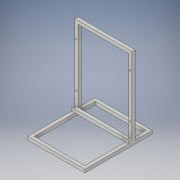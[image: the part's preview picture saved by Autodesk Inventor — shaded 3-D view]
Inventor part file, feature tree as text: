
AUTODESK INVENTOR PART (.ipt)
format: ipt  version: 2019 (Build 230136000, 136)  size: 188,416 bytes
history: native  units: mm
features: extrude x6, sketch x6
ambient origin geometry x8: Origin, YZ Plane, XZ Plane, XY Plane, X Axis, Y Axis, Z Axis, Center Point
bodies: Solid1 (feature_tree)
feature tree (12):
  extrude  "Extrusion1"  Depth=19.0mm
  extrude  "Extrusion2"  Depth=19.0mm
  extrude  "Extrusion3"  Depth=335.0mm
  extrude  "Extrusion4"  Depth=19.0mm
  extrude  "Extrusion5"  Depth=100.0mm
  extrude  "Extrusion6"  Depth=19.0mm
  sketch  "Sketch1"  dims[d2=19.0mm d3=19.0mm]
  sketch  "Sketch3"  dims[d4=19.0mm d5=19.0mm]
  sketch  "Sketch4"  dims[d6=395.0mm d7=335.0mm]
  sketch  "Sketch5"  dims[d8=19.0mm d9=0.0mm d26=19.0mm]
  sketch  "Sketch6"  dims[d27=19.0mm d28=100.0mm]
  sketch  "Sketch7"  dims[d29=460.0mm d30=0.0mm d31=19.0mm d32=316.0mm d33=0.0mm d34=8.0mm d35=8.0mm d36=8.0mm d37=8.0mm d38=9.5mm d39=100.0mm d40=100.0mm d41=9.5mm d42=9.5mm d43=100.0mm d44=100.0mm d45=9.5mm d46=19.0mm d47=0.0mm d48=19.0mm d49=335.0mm d51=119.0mm d52=19.0mm d53=0.0mm d54=8.0mm d55=8.0mm d56=9.5mm d57=9.5mm d58=9.5mm d59=9.5mm d60=39.0mm d61=0.0mm]
